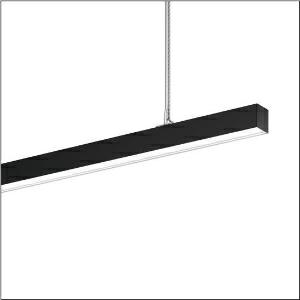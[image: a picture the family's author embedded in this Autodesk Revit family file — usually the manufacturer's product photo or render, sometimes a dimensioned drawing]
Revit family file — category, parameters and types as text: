
# Revit family: silica_21_51mx30dc39bb
name_source: partatom
category: Lighting Fixtures
units: mm (PartAtom-declared; Revit-internal decimal feet)

## family parameters
Cut with Voids When Loaded = No
Host = Face
Light Source = No
Part Type = Normal
Room Calculation Point = No
Round Connector Dimension = Use Diameter
Shared = No

## types (1)
- --- (1 x LED, 10520 lm, 68.3 W, 3000K)
    Apparent Load = 68 VA
    CIE Flux Codes = 47 79 96 57 100
    Color Rendering = 80
    Color Temperature = 3000K
    Default Elevation = 1800 mm
    Description = Silica 21, office luminaire, primary optical cover: cover, of PMMA, opal, light emission: direct/indirect distribution, primary light characteristic: symmetric, installation type: suspended mounting, LED, rated luminous flux: 10.520lm, luminous efficacy: 154lm/W, light colour: 830, colour temperature: 3000K, control gear: DALI 2, with terminal, 3+2-pole, max. 2.5mm², mains connection: 220..240V, AC, 50/60Hz, rated input power: 68.3W, luminaire housing, of aluminium, matt jet black (RAL 9005), length: 3.004mm, width: 53mm, height: 53mm, protection rating (complete): IP20, insulation class (complete): insulation class I (protective earthing), certification: CE, permissible operating ambient temperature: 0..+35°C, standard: EN 50419, packaging unit: 1 piece
    Height = 53 mm
    Lamp = 1 x LED
    Lamp Light Flux = 10520 lm
    Lamp Power = 68.3 W
    Lamp count = 1
    Length = 3004 mm
    Luminous efficacy = 154 lm/W
    Manufacturer = Siteco
    ModVariant = No
    Model = 51MX30DC39BB
    Mounting Place = Ceiling
    Mounting Type = Pendant
    Number of Poles = 1
    OnlyDefault = Yes
    Power Factor = 1
    Product Name = Silica 21
    Product group = office luminaire | ceiling pendant
    ProductGroupID = 903
    Protection Class = Protection class I
    Protection Degree = IP 20
    RLX_Detail_Level = 1
    RLX_Emergency_Light_Flux = 0 lm
    RLX_Emergency_Type = 0
    RLX_Emergency_Type_DB = No
    RlxData = <blob elided: 26157 chars, md5=8aad797c>
    Socket = socket
    Standby Power = 0 W
    System Light Flux = 10520 lm
    System Power = 68 W
    Type Comments = factory setting: luminous flux: 100 % | dim-lin: 254 | 233 mA
    Type Image = l_1335856.jpg
    URL = http://relux.com
    VarID = @adj_118949
    Voltage = 0 V
    Weight = 0.00 kg
    Width = 53 mm

## geometry (parser evidence)
native form markers: Blend x4, Sweep x15
no freeform markers — native parametric forms only
